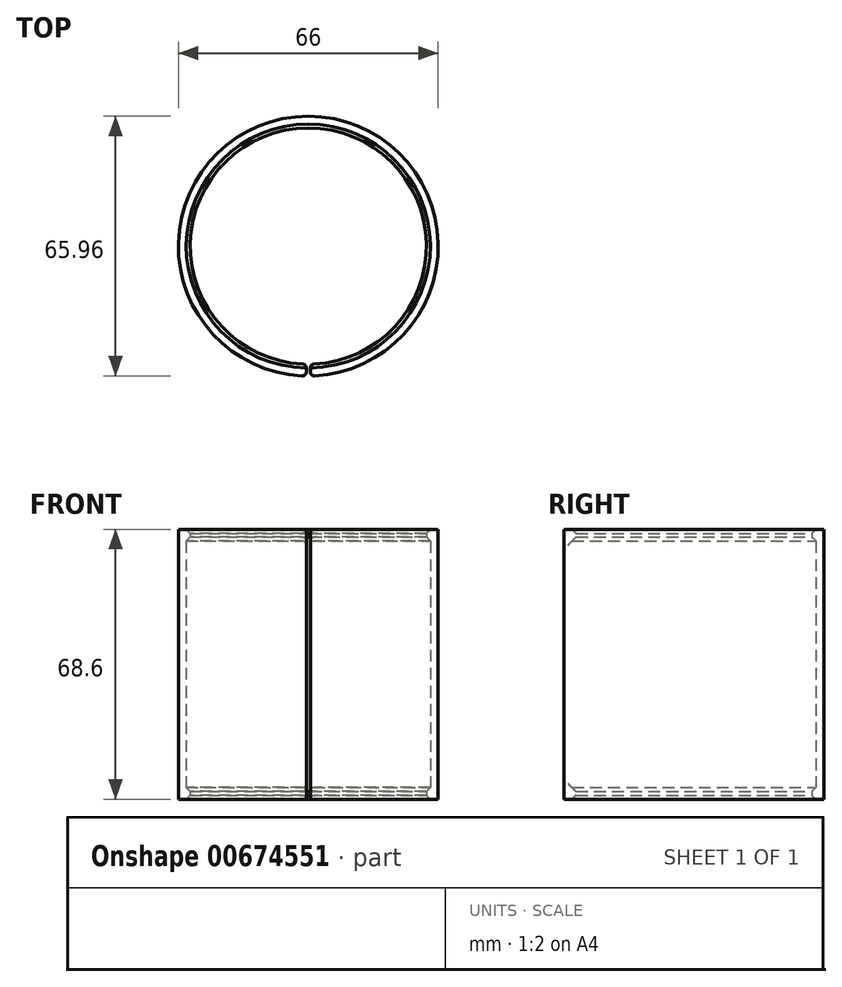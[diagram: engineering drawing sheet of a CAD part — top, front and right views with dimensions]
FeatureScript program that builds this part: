
annotation { "Feature Type Name" : "Feature", "Feature Type Description" : "" }
export const myFeature = defineFeature(function(context is Context, id is Id, definition is map)
    precondition{}
    {
        {
            var Q0;
            Q0=qCreatedBy(makeId("Front.planeOp"),FACE);
            var sketch = newSketch(context, id + "F0", { "sketchPlane" : qUnion([Q0])});
            skLineSegment(sketch, "E0", {"start": v(-33, 0) * mm, "end": v(-33, -34.3) * mm});
            skLineSegment(sketch, "E1", {"start": v(-33, -34.3) * mm, "end": v(-31, -34.3) * mm});
            skLineSegment(sketch, "E2", {"start": v(-31, -34.3) * mm, "end": v(-30, -33.3) * mm});
            skLineSegment(sketch, "E3", {"start": v(-30, -33.3) * mm, "end": v(-30, -32.3) * mm});
            skLineSegment(sketch, "E4", {"start": v(-30, -32.3) * mm, "end": v(-31, -31.3) * mm});
            skLineSegment(sketch, "E5", {"start": v(-31, -31.3) * mm, "end": v(-31, 0) * mm});
            skLineSegment(sketch, "E6", {"start": v(-31, 0) * mm, "end": v(-33, 0) * mm});
            skLineSegment(sketch, "E7", {"start": v(0, 0) * mm, "end": v(-33, 0) * mm, "construction": true});
            skLineSegment(sketch, "E8.MirrorCS", {"start": v(-30, 33.3) * mm, "end": v(-30, 32.3) * mm});
            skLineSegment(sketch, "E9.MirrorCS", {"start": v(-31, 34.3) * mm, "end": v(-30, 33.3) * mm});
            skLineSegment(sketch, "E10.MirrorCS", {"start": v(-30, 32.3) * mm, "end": v(-31, 31.3) * mm});
            skLineSegment(sketch, "E11.MirrorCS", {"start": v(-33, 0) * mm, "end": v(-33, 34.3) * mm});
            skLineSegment(sketch, "E12.MirrorCS", {"start": v(-31, 31.3) * mm, "end": v(-31, 0) * mm});
            skLineSegment(sketch, "E13.MirrorCS", {"start": v(-33, 34.3) * mm, "end": v(-31, 34.3) * mm});
            skLineSegment(sketch, "E14", {"start": v(0, 0) * mm, "end": v(0, 34.3) * mm, "construction": true});
            skSolve(sketch);
        }
        {
            var Q0;
            Q0=makeQuery(id+"F0.imprint","IMPRINT",FACE,{"disambiguationData":[TD([[makeQuery(id+"F0.imprint","IMPRINT",EDGE,{"derivedFrom":sQuery(id+"F0.wireOp",EDGE,"E8.MirrorCS")}),-1.0]])]});
            var Q1;
            Q1=makeQuery(id+"F0.imprint","IMPRINT",FACE,{"disambiguationData":[TD([[makeQuery(id+"F0.imprint","IMPRINT",EDGE,{"derivedFrom":sQuery(id+"F0.wireOp",EDGE,"E0")}),1.0]])]});
            var Q2;
            Q2=sQuery(id+"F0.wireOp",EDGE,"E14");
            revolve(context, id + "F1", {"entities" : qUnion([Q0, Q1]), "axis" : qUnion([Q2]), "revolveType" : RevolveType.FULL});
        }
        {
            var Q0;
            Q0=makeQuery(id+"F1.opRevolve","SWEPT_FACE",FACE,{"disambiguationData":[OSD([sQuery(id+"F0.wireOp",EDGE,"E13.MirrorCS")])]});
            var sketch = newSketch(context, id + "F2", { "sketchPlane" : qUnion([Q0])});
            skLineSegment(sketch, "E15.bottom", {"start": v(-0.5, 0) * mm, "end": v(0.5, 0) * mm});
            skLineSegment(sketch, "E15.top", {"start": v(-0.5, -40) * mm, "end": v(0.5, -40) * mm});
            skLineSegment(sketch, "E15.left", {"start": v(-0.5, 0) * mm, "end": v(-0.5, -40) * mm});
            skLineSegment(sketch, "E15.right", {"start": v(0.5, 0) * mm, "end": v(0.5, -40) * mm});
            skPoint(sketch, "E15.middle", {"position": v(0, -20) * mm});
            skSolve(sketch);
        }
        {
            var Q0;
            Q0 = qSketchRegion(id + "F2", true);
            extrude(context, id + "F3", {"entities" : qUnion([Q0]), "operationType" : NewBodyOperationType.REMOVE, "endBound" : BoundingType.THROUGH_ALL, "oppositeDirection" : true, "depth" : 25 * mm, "offsetDistance" : 25 * mm});
        }
        {
            var Q0;
            Q0=makeQuery(id+"F3.boolean.opBoolean","INTERSECT",EDGE,{"derivedFrom":[makeQuery(id+"F1.opRevolve","SWEPT_FACE",FACE,{"disambiguationData":[OSD([sQuery(id+"F0.wireOp",EDGE,"E0"),sQuery(id+"F0.wireOp",EDGE,"E11.MirrorCS")])]}),makeQuery(id+"F3.opExtrude","SWEPT_FACE",FACE,{"disambiguationData":[OSD([sQuery(id+"F2.wireOp",EDGE,"E15.left")])]})]});
            var Q1;
            Q1=makeQuery(id+"F3.boolean.opBoolean","INTERSECT",EDGE,{"derivedFrom":[makeQuery(id+"F1.opRevolve","SWEPT_FACE",FACE,{"disambiguationData":[OSD([sQuery(id+"F0.wireOp",EDGE,"E5"),sQuery(id+"F0.wireOp",EDGE,"E12.MirrorCS")])]}),makeQuery(id+"F3.opExtrude","SWEPT_FACE",FACE,{"disambiguationData":[OSD([sQuery(id+"F2.wireOp",EDGE,"E15.left")])]})]});
            var Q2;
            Q2=makeQuery(id+"F3.boolean.opBoolean","INTERSECT",EDGE,{"derivedFrom":[makeQuery(id+"F1.opRevolve","SWEPT_FACE",FACE,{"disambiguationData":[OSD([sQuery(id+"F0.wireOp",EDGE,"E8.MirrorCS")])]}),makeQuery(id+"F3.opExtrude","SWEPT_FACE",FACE,{"disambiguationData":[OSD([sQuery(id+"F2.wireOp",EDGE,"E15.left")])]})]});
            var Q3;
            Q3=makeQuery(id+"F3.boolean.opBoolean","INTERSECT",EDGE,{"derivedFrom":[makeQuery(id+"F1.opRevolve","SWEPT_FACE",FACE,{"disambiguationData":[OSD([sQuery(id+"F0.wireOp",EDGE,"E3")])]}),makeQuery(id+"F3.opExtrude","SWEPT_FACE",FACE,{"disambiguationData":[OSD([sQuery(id+"F2.wireOp",EDGE,"E15.left")])]})]});
            var Q4;
            Q4=makeQuery(id+"F3.boolean.opBoolean","INTERSECT",EDGE,{"derivedFrom":[makeQuery(id+"F1.opRevolve","SWEPT_FACE",FACE,{"disambiguationData":[OSD([sQuery(id+"F0.wireOp",EDGE,"E3")])]}),makeQuery(id+"F3.opExtrude","SWEPT_FACE",FACE,{"disambiguationData":[OSD([sQuery(id+"F2.wireOp",EDGE,"E15.right")])]})]});
            var Q5;
            Q5=makeQuery(id+"F3.boolean.opBoolean","INTERSECT",EDGE,{"derivedFrom":[makeQuery(id+"F1.opRevolve","SWEPT_FACE",FACE,{"disambiguationData":[OSD([sQuery(id+"F0.wireOp",EDGE,"E5"),sQuery(id+"F0.wireOp",EDGE,"E12.MirrorCS")])]}),makeQuery(id+"F3.opExtrude","SWEPT_FACE",FACE,{"disambiguationData":[OSD([sQuery(id+"F2.wireOp",EDGE,"E15.right")])]})]});
            var Q6;
            Q6=makeQuery(id+"F3.boolean.opBoolean","INTERSECT",EDGE,{"derivedFrom":[makeQuery(id+"F1.opRevolve","SWEPT_FACE",FACE,{"disambiguationData":[OSD([sQuery(id+"F0.wireOp",EDGE,"E8.MirrorCS")])]}),makeQuery(id+"F3.opExtrude","SWEPT_FACE",FACE,{"disambiguationData":[OSD([sQuery(id+"F2.wireOp",EDGE,"E15.right")])]})]});
            var Q7;
            Q7=makeQuery(id+"F3.boolean.opBoolean","INTERSECT",EDGE,{"derivedFrom":[makeQuery(id+"F1.opRevolve","SWEPT_FACE",FACE,{"disambiguationData":[OSD([sQuery(id+"F0.wireOp",EDGE,"E0"),sQuery(id+"F0.wireOp",EDGE,"E11.MirrorCS")])]}),makeQuery(id+"F3.opExtrude","SWEPT_FACE",FACE,{"disambiguationData":[OSD([sQuery(id+"F2.wireOp",EDGE,"E15.right")])]})]});
            fillet(context, id + "F4", {"entities" : qUnion([Q0, Q1, Q2, Q3, Q4, Q5, Q6, Q7]), "radius" : 1 * mm, "tangentPropagation" : true, "allowEdgeOverflow" : false});
        }
    });
